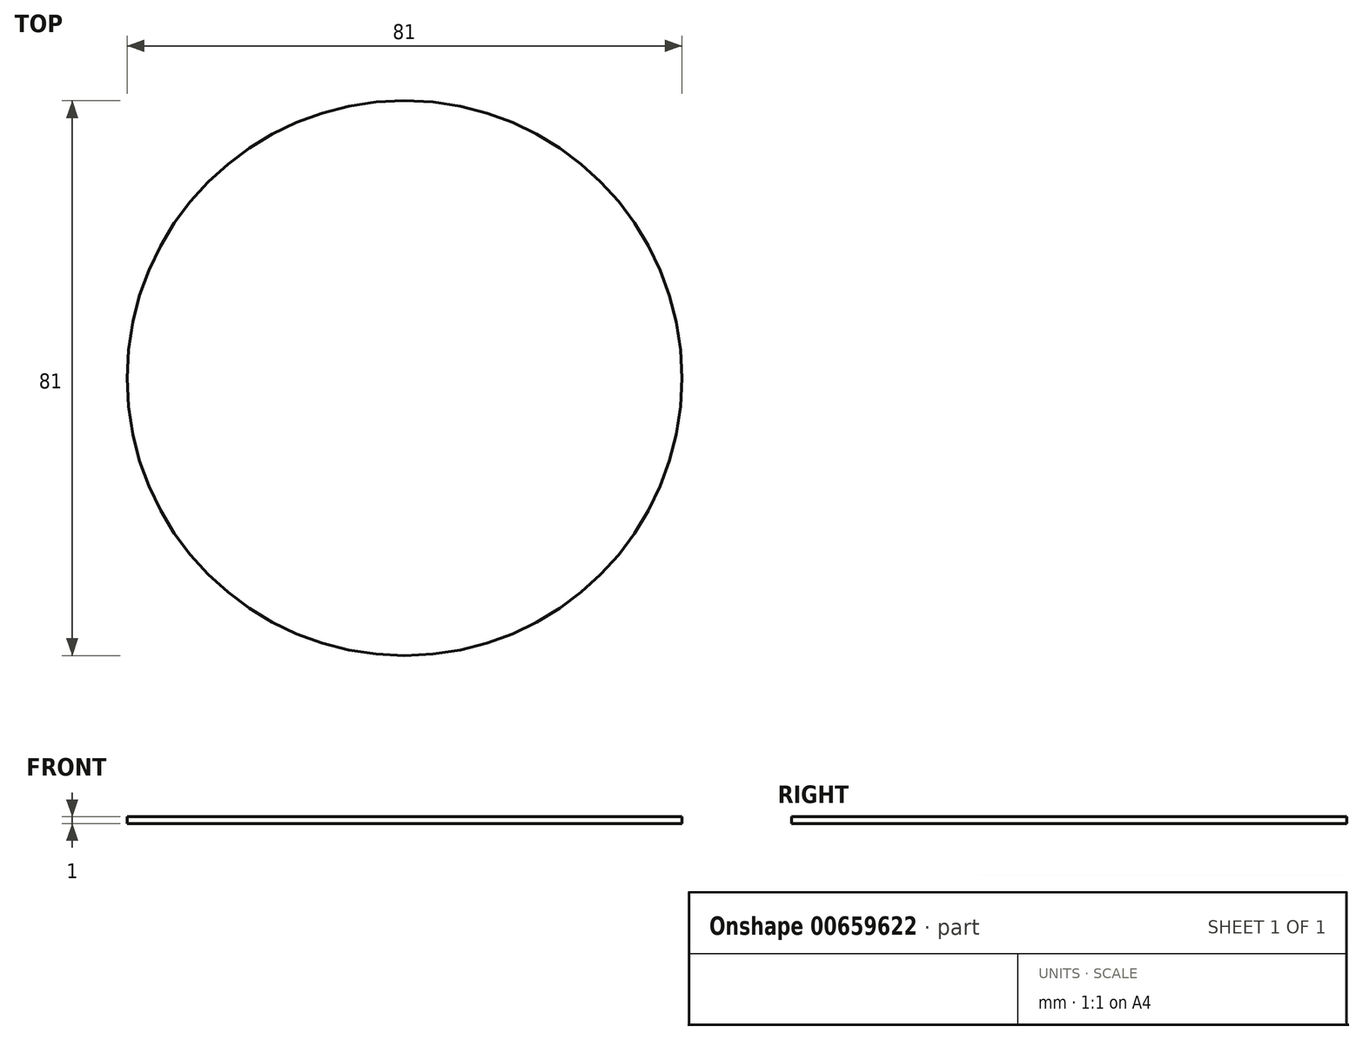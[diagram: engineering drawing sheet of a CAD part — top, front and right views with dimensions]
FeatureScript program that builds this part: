
annotation { "Feature Type Name" : "Feature", "Feature Type Description" : "" }
export const myFeature = defineFeature(function(context is Context, id is Id, definition is map)
    precondition{}
    {
        {
            var Q0;
            Q0=qCreatedBy(makeId("Top.planeOp"),FACE);
            var sketch = newSketch(context, id + "F0", { "sketchPlane" : qUnion([Q0])});
            skCircle(sketch, "E0", {"center": v(0, 0) * mm, "radius": 40.5 * mm});
            skSolve(sketch);
        }
        {
            var Q0;
            Q0 = qSketchRegion(id + "F0", true);
            extrude(context, id + "F1", {"entities" : qUnion([Q0]), "depth" : 1 * mm, "offsetDistance" : 25.4 * mm});
        }
    });
